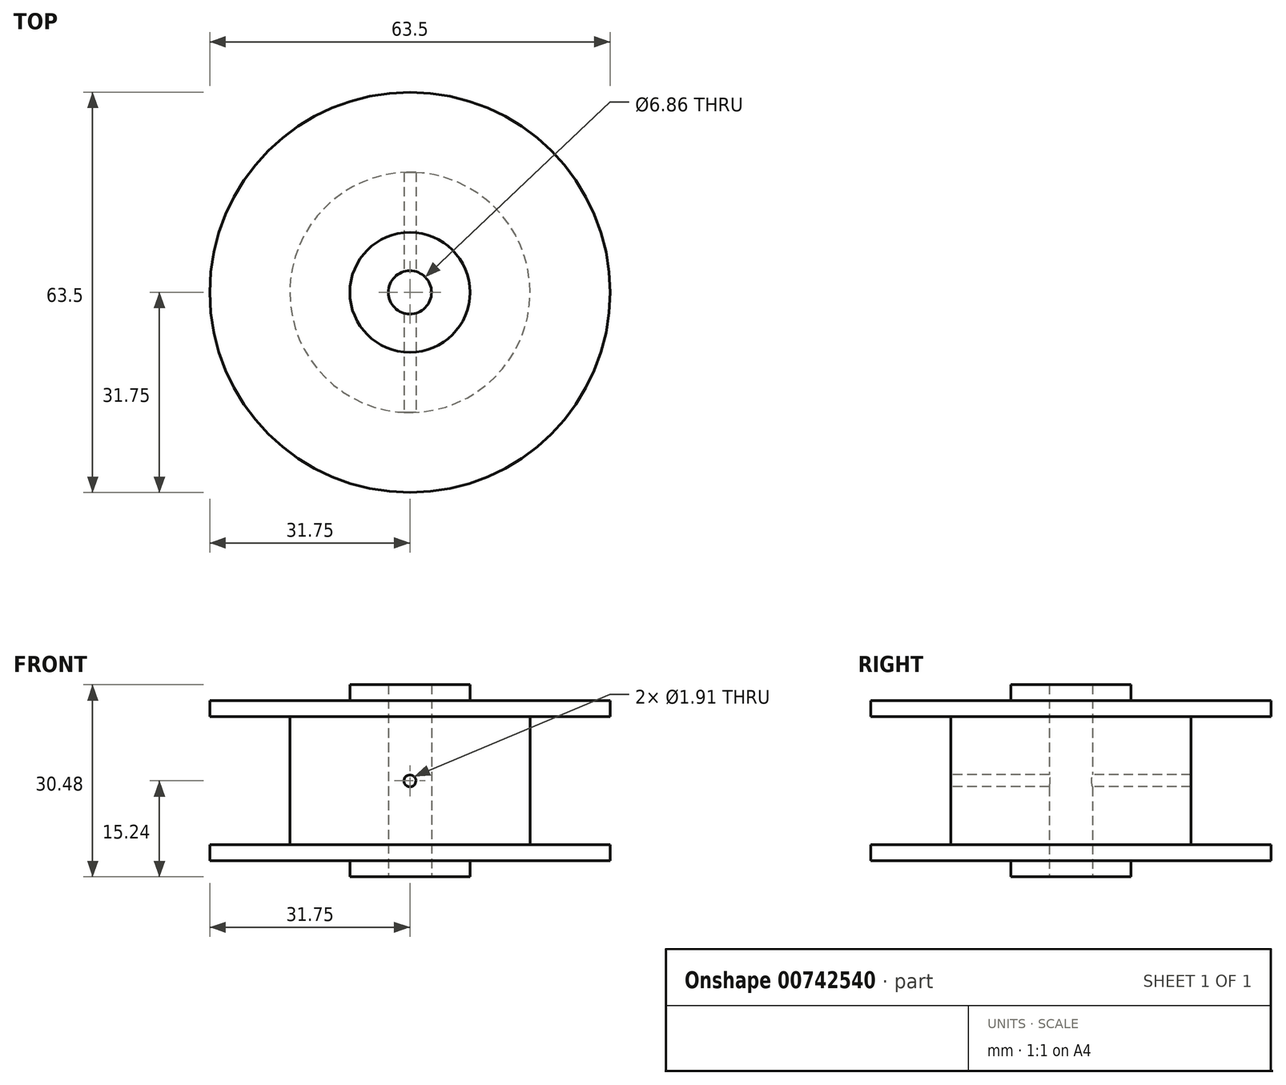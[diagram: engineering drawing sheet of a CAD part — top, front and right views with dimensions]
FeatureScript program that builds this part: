
annotation { "Feature Type Name" : "Feature", "Feature Type Description" : "" }
export const myFeature = defineFeature(function(context is Context, id is Id, definition is map)
    precondition{}
    {
        {
            var Q0;
            Q0=qCreatedBy(makeId("Top.planeOp"),FACE);
            var sketch = newSketch(context, id + "F0", { "sketchPlane" : qUnion([Q0])});
            skCircle(sketch, "E0", {"center": v(0, 0) * mm, "radius": 31.75 * mm});
            skSolve(sketch);
        }
        {
            var Q0;
            Q0=makeQuery(id+"F0.imprint","IMPRINT",FACE,{"disambiguationData":[TD([[makeQuery(id+"F0.imprint","IMPRINT",EDGE,{"derivedFrom":sQuery(id+"F0.wireOp",EDGE,"E0")}),1.0]])]});
            extrude(context, id + "F1", {"entities" : qUnion([Q0]), "depth" : 2.54 * mm, "offsetDistance" : 25.4 * mm});
        }
        {
            var Q0;
            Q0=makeQuery(id+"F1.opExtrude","CAP_FACE",FACE,{"disambiguationData":[OSD([sQuery(id+"F0.wireOp",EDGE,"E0")])],"isStart":false});
            var sketch = newSketch(context, id + "F2", { "sketchPlane" : qUnion([Q0])});
            skCircle(sketch, "E1", {"center": v(0, 0) * mm, "radius": 19.05 * mm});
            skSolve(sketch);
        }
        {
            var Q0;
            Q0=makeQuery(id+"F2.imprint","IMPRINT",FACE,{"disambiguationData":[TD([[makeQuery(id+"F2.imprint","IMPRINT",EDGE,{"derivedFrom":sQuery(id+"F2.wireOp",EDGE,"E1")}),1.0]])]});
            extrude(context, id + "F3", {"entities" : qUnion([Q0]), "operationType" : NewBodyOperationType.ADD, "depth" : 20.32 * mm, "offsetDistance" : 25.4 * mm});
        }
        {
            var Q0;
            Q0=makeQuery(id+"F3.opExtrude","CAP_FACE",FACE,{"disambiguationData":[OSD([sQuery(id+"F2.wireOp",EDGE,"E1")])],"isStart":false});
            var sketch = newSketch(context, id + "F4", { "sketchPlane" : qUnion([Q0])});
            skCircle(sketch, "E2", {"center": v(0, 0) * mm, "radius": 31.75 * mm});
            skSolve(sketch);
        }
        {
            var Q0;
            Q0=makeQuery(id+"F4.imprint","IMPRINT",FACE,{"disambiguationData":[TD([[makeQuery(id+"F4.imprint","IMPRINT",EDGE,{"derivedFrom":sQuery(id+"F4.wireOp",EDGE,"E2")}),1.0]])]});
            var Q1;
            Q1=makeQuery(id+"F4.imprint","IMPRINT",FACE,{"disambiguationData":[TD([[makeQuery(id+"F4.imprint","IMPRINT",EDGE,{"derivedFrom":makeQuery(id+"F3.opExtrude","CAP_EDGE",EDGE,{"disambiguationData":[OSD([sQuery(id+"F2.wireOp",EDGE,"E1")])],"isStart":false})}),1.0]])]});
            extrude(context, id + "F5", {"entities" : qUnion([Q0, Q1]), "operationType" : NewBodyOperationType.ADD, "depth" : 2.54 * mm, "offsetDistance" : 25.4 * mm});
        }
        {
            var Q0;
            Q0=makeQuery(id+"F5.opExtrude","CAP_FACE",FACE,{"disambiguationData":[OSD([sQuery(id+"F4.wireOp",EDGE,"E2")])],"isStart":false});
            var sketch = newSketch(context, id + "F6", { "sketchPlane" : qUnion([Q0])});
            skCircle(sketch, "E3", {"center": v(0, 0) * mm, "radius": 9.53 * mm});
            skSolve(sketch);
        }
        {
            var Q0;
            Q0 = qSketchRegion(id + "F6", true);
            extrude(context, id + "F7", {"entities" : qUnion([Q0]), "operationType" : NewBodyOperationType.ADD, "depth" : 2.54 * mm, "offsetDistance" : 25.4 * mm});
        }
        {
            var Q0;
            Q0=makeQuery(id+"F1.opExtrude","CAP_FACE",FACE,{"disambiguationData":[OSD([sQuery(id+"F0.wireOp",EDGE,"E0")])],"isStart":true});
            var sketch = newSketch(context, id + "F8", { "sketchPlane" : qUnion([Q0])});
            skCircle(sketch, "E4", {"center": v(0, 0) * mm, "radius": 9.53 * mm});
            skSolve(sketch);
        }
        {
            var Q0;
            Q0=makeQuery(id+"F8.imprint","IMPRINT",FACE,{"disambiguationData":[TD([[makeQuery(id+"F8.imprint","IMPRINT",EDGE,{"derivedFrom":sQuery(id+"F8.wireOp",EDGE,"E4")}),1.0]])]});
            extrude(context, id + "F9", {"entities" : qUnion([Q0]), "operationType" : NewBodyOperationType.ADD, "depth" : 2.54 * mm, "offsetDistance" : 25.4 * mm});
        }
        {
            var Q0;
            Q0=makeQuery(id+"F9.opExtrude","CAP_FACE",FACE,{"disambiguationData":[OSD([sQuery(id+"F8.wireOp",EDGE,"E4")])],"isStart":false});
            var sketch = newSketch(context, id + "F10", { "sketchPlane" : qUnion([Q0])});
            skCircle(sketch, "E5", {"center": v(0, 0) * mm, "radius": 3.43 * mm});
            skSolve(sketch);
        }
        {
            var Q0;
            Q0=makeQuery(id+"F10.imprint","IMPRINT",FACE,{"disambiguationData":[TD([[makeQuery(id+"F10.imprint","IMPRINT",EDGE,{"derivedFrom":sQuery(id+"F10.wireOp",EDGE,"E5")}),1.0]])]});
            extrude(context, id + "F11", {"entities" : qUnion([Q0]), "operationType" : NewBodyOperationType.REMOVE, "oppositeDirection" : true, "depth" : 30.48 * mm, "offsetDistance" : 25.4 * mm});
        }
        {
            var Q0;
            Q0=qCreatedBy(makeId("Front.planeOp"),FACE);
            var sketch = newSketch(context, id + "F12", { "sketchPlane" : qUnion([Q0])});
            skCircle(sketch, "E6", {"center": v(0, 12.7) * mm, "radius": 0.95 * mm});
            skSolve(sketch);
        }
        {
            var Q0;
            Q0 = qSketchRegion(id + "F12", true);
            extrude(context, id + "F13", {"entities" : qUnion([Q0]), "operationType" : NewBodyOperationType.REMOVE, "oppositeDirection" : true, "depth" : 25.4 * mm, "offsetDistance" : 25.4 * mm, "hasSecondDirection" : true, "secondDirectionOppositeDirection" : false, "secondDirectionDepth" : 25.4 * mm});
        }
    });
